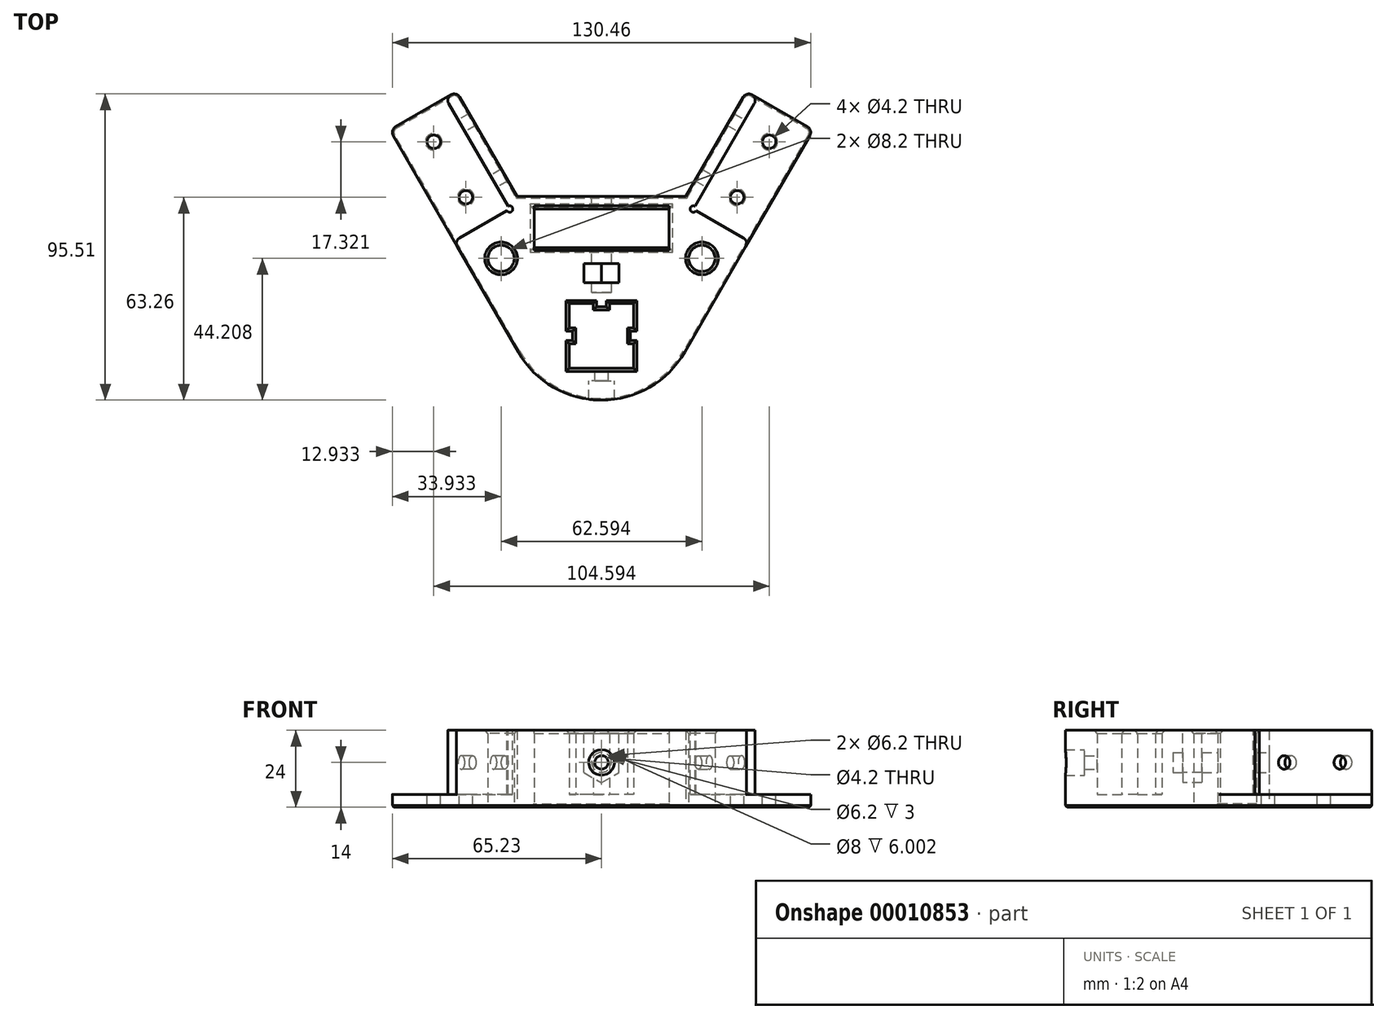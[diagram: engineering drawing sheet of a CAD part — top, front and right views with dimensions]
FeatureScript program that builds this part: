
annotation { "Feature Type Name" : "Feature", "Feature Type Description" : "" }
export const myFeature = defineFeature(function(context is Context, id is Id, definition is map)
    precondition{}
    {
        {
            var Q0;
            Q0=qCreatedBy(makeId("Top.planeOp"),FACE);
            var sketch = newSketch(context, id + "F0", { "sketchPlane" : qUnion([Q0])});
            skLineSegment(sketch, "E0.rect.bottom", {"start": v(10.05, -10.05) * mm, "end": v(-10.05, -10.05) * mm});
            skLineSegment(sketch, "E0.rect.top", {"start": v(10.05, 10.05) * mm, "end": v(-10.05, 10.05) * mm});
            skLineSegment(sketch, "E0.rect.left", {"start": v(10.05, -10.05) * mm, "end": v(10.05, 10.05) * mm});
            skLineSegment(sketch, "E0.rect.right", {"start": v(-10.05, -10.05) * mm, "end": v(-10.05, 10.05) * mm});
            skPoint(sketch, "E0.rect.middle", {"position": v(0, 0) * mm});
            skLineSegment(sketch, "E1", {"start": v(-10.05, -2.5) * mm, "end": v(-8.05, -2.5) * mm});
            skLineSegment(sketch, "E2", {"start": v(-8.05, -2.5) * mm, "end": v(-8.05, 2.5) * mm});
            skLineSegment(sketch, "E3", {"start": v(-8.05, 2.5) * mm, "end": v(-10.05, 2.5) * mm});
            skLineSegment(sketch, "E4", {"start": v(-2.5, 10.05) * mm, "end": v(-2.5, 8.05) * mm});
            skLineSegment(sketch, "E5", {"start": v(-2.5, 8.05) * mm, "end": v(2.5, 8.05) * mm});
            skLineSegment(sketch, "E6", {"start": v(2.5, 8.05) * mm, "end": v(2.5, 10.05) * mm});
            skLineSegment(sketch, "E7", {"start": v(10.05, 2.5) * mm, "end": v(8.05, 2.5) * mm});
            skLineSegment(sketch, "E8", {"start": v(8.05, 2.5) * mm, "end": v(8.05, -2.5) * mm});
            skLineSegment(sketch, "E9", {"start": v(8.05, -2.5) * mm, "end": v(10.05, -2.5) * mm});
            skLineSegment(sketch, "E10", {"start": v(-25.98, -5.05) * mm, "end": v(-65.96, 64.2) * mm});
            skLineSegment(sketch, "E11", {"start": v(-65.96, 64.2) * mm, "end": v(-45.17, 76.2) * mm});
            skLineSegment(sketch, "E12", {"start": v(-45.17, 76.2) * mm, "end": v(-25.17, 41.55) * mm});
            skLineSegment(sketch, "E13", {"start": v(-25.17, 41.55) * mm, "end": v(25.17, 41.55) * mm});
            skLineSegment(sketch, "E14", {"start": v(25.17, 41.55) * mm, "end": v(45.17, 76.2) * mm});
            skLineSegment(sketch, "E15", {"start": v(45.17, 76.2) * mm, "end": v(65.96, 64.2) * mm});
            skLineSegment(sketch, "E16", {"start": v(65.96, 64.2) * mm, "end": v(25.98, -5.05) * mm});
            skPoint(sketch, "E17.visualSharp", {"position": v(0, -50.05) * mm});
            skArc(sketch, "E17.filletArc", {"start": v(-25.98, -5.05) * mm, "mid": v(0, -20.05) * mm, "end": v(25.98, -5.05) * mm});
            skLineSegment(sketch, "E18", {"start": v(-48.64, 74.2) * mm, "end": v(-28.64, 39.55) * mm});
            skLineSegment(sketch, "E19", {"start": v(-28.64, 39.55) * mm, "end": v(-45.96, 29.55) * mm});
            skLineSegment(sketch, "E20", {"start": v(48.64, 74.2) * mm, "end": v(28.64, 39.55) * mm});
            skLineSegment(sketch, "E21", {"start": v(28.64, 39.55) * mm, "end": v(45.96, 29.55) * mm});
            skLineSegment(sketch, "E22", {"start": v(-28.64, 39.55) * mm, "end": v(-25.17, 41.55) * mm, "construction": true});
            skLineSegment(sketch, "E23", {"start": v(-57.3, 69.2) * mm, "end": v(-37.3, 34.55) * mm, "construction": true});
            skCircle(sketch, "E24", {"center": v(-52.3, 60.53) * mm, "radius": 2.1 * mm});
            skCircle(sketch, "E25", {"center": v(-42.3, 43.21) * mm, "radius": 2.1 * mm});
            skCircle(sketch, "E26", {"center": v(52.3, 60.53) * mm, "radius": 2.1 * mm});
            skCircle(sketch, "E27", {"center": v(42.3, 43.21) * mm, "radius": 2.1 * mm});
            skLineSegment(sketch, "E28", {"start": v(-21, 39.55) * mm, "end": v(21, 39.55) * mm});
            skLineSegment(sketch, "E29", {"start": v(21, 39.55) * mm, "end": v(21, 27.55) * mm});
            skLineSegment(sketch, "E30", {"start": v(10.05, 15.05) * mm, "end": v(-10.05, 15.05) * mm});
            skLineSegment(sketch, "E31", {"start": v(-21, 27.55) * mm, "end": v(-21, 39.55) * mm});
            skLineSegment(sketch, "E32", {"start": v(-21, 27.55) * mm, "end": v(-18.6, 17.84) * mm});
            skLineSegment(sketch, "E33", {"start": v(-18.6, 17.84) * mm, "end": v(-10.05, 15.05) * mm});
            skLineSegment(sketch, "E34", {"start": v(21, 27.55) * mm, "end": v(18.6, 17.84) * mm});
            skLineSegment(sketch, "E35", {"start": v(18.6, 17.84) * mm, "end": v(10.05, 15.05) * mm});
            skLineSegment(sketch, "E36", {"start": v(-37.3, 34.55) * mm, "end": v(-20.27, 5.06) * mm, "construction": true});
            skCircle(sketch, "E37", {"center": v(-31.3, 24.16) * mm, "radius": 4.1 * mm});
            skLineSegment(sketch, "E38", {"start": v(0, -71.13) * mm, "end": v(0, 233.1) * mm, "construction": true});
            skCircle(sketch, "E39", {"center": v(31.3, 24.16) * mm, "radius": 4.1 * mm});
            skLineSegment(sketch, "E40", {"start": v(-26.33, 43.55) * mm, "end": v(26.33, 43.55) * mm});
            skLineSegment(sketch, "E41", {"start": v(-21, 27.55) * mm, "end": v(21, 27.55) * mm});
            skLineSegment(sketch, "E42", {"start": v(-19.77, 22.55) * mm, "end": v(19.77, 22.55) * mm});
            skSolve(sketch);
        }
        {
            var Q0;
            {var subQ2=sQuery(id+"F0.wireOp",EDGE,"E13");Q0=makeQuery(id+"F0.imprint","IMPRINT",FACE,{"disambiguationData":[TD([[makeQuery(id+"F0.imprint","IMPRINT",EDGE,{"derivedFrom":subQ2}),1.0]])]});}
            var Q1;
            {var subQ16=sQuery(id+"F0.wireOp",EDGE,"E0.rect.bottom");Q1=makeQuery(id+"F0.imprint","IMPRINT",FACE,{"disambiguationData":[TD([[makeQuery(id+"F0.imprint","IMPRINT",EDGE,{"derivedFrom":subQ16}),1.0]])]});}
            var Q2;
            {var subQ1=sQuery(id+"F0.wireOp",EDGE,"E1");Q2=makeQuery(id+"F0.imprint","IMPRINT",FACE,{"disambiguationData":[TD([[makeQuery(id+"F0.imprint","IMPRINT",EDGE,{"derivedFrom":subQ1}),1.0]])]});}
            var Q3;
            {var subQ1=sQuery(id+"F0.wireOp",EDGE,"E4");Q3=makeQuery(id+"F0.imprint","IMPRINT",FACE,{"disambiguationData":[TD([[makeQuery(id+"F0.imprint","IMPRINT",EDGE,{"derivedFrom":subQ1}),1.0]])]});}
            var Q4;
            {var subQ1=sQuery(id+"F0.wireOp",EDGE,"E7");Q4=makeQuery(id+"F0.imprint","IMPRINT",FACE,{"disambiguationData":[TD([[makeQuery(id+"F0.imprint","IMPRINT",EDGE,{"derivedFrom":subQ1}),1.0]])]});}
            var Q5;
            {var subQ1=sQuery(id+"F0.wireOp",EDGE,"E41");Q5=makeQuery(id+"F0.imprint","IMPRINT",FACE,{"disambiguationData":[TD([[makeQuery(id+"F0.imprint","IMPRINT",EDGE,{"derivedFrom":subQ1}),-1.0]])]});}
            var Q6;
            Q6=makeQuery(id+"F0.imprint","IMPRINT",FACE,{"disambiguationData":[TD([[makeQuery(id+"F0.imprint","IMPRINT",EDGE,{"derivedFrom":sQuery(id+"F0.wireOp",EDGE,"E30")}),-1.0]])]});
            extrude(context, id + "F1", {"entities" : qUnion([Q0, Q1, Q2, Q3, Q4, Q5, Q6]), "depth" : 20 * mm});
        }
        {
            var Q0;
            {var subQ0=sQuery(id+"F0.wireOp",EDGE,"E20");Q0=makeQuery(id+"F0.imprint","IMPRINT",FACE,{"disambiguationData":[TD([[makeQuery(id+"F0.imprint","IMPRINT",EDGE,{"derivedFrom":subQ0}),1.0]])]});}
            var Q1;
            {var subQ16=sQuery(id+"F0.wireOp",EDGE,"E0.rect.bottom");Q1=makeQuery(id+"F0.imprint","IMPRINT",FACE,{"disambiguationData":[TD([[makeQuery(id+"F0.imprint","IMPRINT",EDGE,{"derivedFrom":subQ16}),1.0]])]});}
            var Q2;
            {var subQ11=sQuery(id+"F0.wireOp",EDGE,"E0.rect.bottom");Q2=makeQuery(id+"F0.imprint","IMPRINT",FACE,{"disambiguationData":[TD([[makeQuery(id+"F0.imprint","IMPRINT",EDGE,{"derivedFrom":subQ11}),-1.0]])]});}
            var Q3;
            {var subQ1=sQuery(id+"F0.wireOp",EDGE,"E18");Q3=makeQuery(id+"F0.imprint","IMPRINT",FACE,{"disambiguationData":[TD([[makeQuery(id+"F0.imprint","IMPRINT",EDGE,{"derivedFrom":subQ1}),-1.0]])]});}
            var Q4;
            {var subQ1=sQuery(id+"F0.wireOp",EDGE,"E4");Q4=makeQuery(id+"F0.imprint","IMPRINT",FACE,{"disambiguationData":[TD([[makeQuery(id+"F0.imprint","IMPRINT",EDGE,{"derivedFrom":subQ1}),1.0]])]});}
            var Q5;
            {var subQ1=sQuery(id+"F0.wireOp",EDGE,"E7");Q5=makeQuery(id+"F0.imprint","IMPRINT",FACE,{"disambiguationData":[TD([[makeQuery(id+"F0.imprint","IMPRINT",EDGE,{"derivedFrom":subQ1}),1.0]])]});}
            var Q6;
            {var subQ1=sQuery(id+"F0.wireOp",EDGE,"E1");Q6=makeQuery(id+"F0.imprint","IMPRINT",FACE,{"disambiguationData":[TD([[makeQuery(id+"F0.imprint","IMPRINT",EDGE,{"derivedFrom":subQ1}),1.0]])]});}
            var Q7;
            {var subQ2=sQuery(id+"F0.wireOp",EDGE,"E13");Q7=makeQuery(id+"F0.imprint","IMPRINT",FACE,{"disambiguationData":[TD([[makeQuery(id+"F0.imprint","IMPRINT",EDGE,{"derivedFrom":subQ2}),1.0]])]});}
            var Q8;
            {var subQ1=sQuery(id+"F0.wireOp",EDGE,"E41");Q8=makeQuery(id+"F0.imprint","IMPRINT",FACE,{"disambiguationData":[TD([[makeQuery(id+"F0.imprint","IMPRINT",EDGE,{"derivedFrom":subQ1}),-1.0]])]});}
            var Q9;
            Q9=makeQuery(id+"F0.imprint","IMPRINT",FACE,{"disambiguationData":[TD([[makeQuery(id+"F0.imprint","IMPRINT",EDGE,{"derivedFrom":sQuery(id+"F0.wireOp",EDGE,"E30")}),-1.0]])]});
            extrude(context, id + "F2", {"entities" : qUnion([Q0, Q1, Q2, Q3, Q4, Q5, Q6, Q7, Q8, Q9]), "operationType" : NewBodyOperationType.ADD, "oppositeDirection" : true, "depth" : 4 * mm});
        }
        {
            var Q0;
            {var subQ0=sQuery(id+"F0.wireOp",EDGE,"E40");Q0=makeQuery(id+"F2.boolean.opBoolean","MERGE",FACE,{"derivedFrom":[makeQuery(id+"F1.opExtrude","SWEPT_FACE",FACE,{"disambiguationData":[OSD([subQ0])]}),makeQuery(id+"F2.opExtrude","SWEPT_FACE",FACE,{"disambiguationData":[OSD([subQ0])]})]});}
            var sketch = newSketch(context, id + "F3", { "sketchPlane" : qUnion([Q0])});
            skCircle(sketch, "E43", {"center": v(0, 10) * mm, "radius": 3.1 * mm});
            skSolve(sketch);
        }
        {
            var Q0;
            Q0=makeQuery(id+"F3.imprint","IMPRINT",FACE,{"disambiguationData":[TD([[makeQuery(id+"F3.imprint","IMPRINT",EDGE,{"derivedFrom":sQuery(id+"F3.wireOp",EDGE,"E43")}),1.0]])]});
            extrude(context, id + "F4", {"entities" : qUnion([Q0]), "operationType" : NewBodyOperationType.REMOVE, "oppositeDirection" : true, "depth" : 30 * mm});
        }
        {
            var Q0;
            Q0=makeQuery(id+"F1.opExtrude","SWEPT_FACE",FACE,{"disambiguationData":[OSD([sQuery(id+"F0.wireOp",EDGE,"E20")])]});
            var sketch = newSketch(context, id + "F5", { "sketchPlane" : qUnion([Q0])});
            skCircle(sketch, "E44", {"center": v(58.57, 10) * mm, "radius": 2.1 * mm});
            skCircle(sketch, "E45", {"center": v(78.57, 10) * mm, "radius": 2.1 * mm});
            skSolve(sketch);
        }
        {
            var Q0;
            Q0=qSketchRegion(id+"F5",true);
            extrude(context, id + "F6", {"entities" : qUnion([Q0]), "operationType" : NewBodyOperationType.REMOVE, "oppositeDirection" : true, "depth" : 25 * mm});
        }
        {
            var Q0;
            Q0=makeQuery(id+"F1.opExtrude","SWEPT_FACE",FACE,{"disambiguationData":[OSD([sQuery(id+"F0.wireOp",EDGE,"E18")])]});
            var sketch = newSketch(context, id + "F7", { "sketchPlane" : qUnion([Q0])});
            skCircle(sketch, "E46", {"center": v(-78.57, 10) * mm, "radius": 2.1 * mm});
            skCircle(sketch, "E47", {"center": v(-58.57, 10) * mm, "radius": 2.1 * mm});
            skSolve(sketch);
        }
        {
            var Q0;
            Q0=qSketchRegion(id+"F7",true);
            extrude(context, id + "F8", {"entities" : qUnion([Q0]), "operationType" : NewBodyOperationType.REMOVE, "oppositeDirection" : true, "depth" : 25 * mm});
        }
        {
            var Q0;
            Q0=makeQuery(id+"F1.opExtrude","CAP_FACE",FACE,{"disambiguationData":[OSD([sQuery(id+"F0.wireOp",EDGE,"E0.rect.bottom"),sQuery(id+"F0.wireOp",EDGE,"E0.rect.top"),sQuery(id+"F0.wireOp",EDGE,"E0.rect.left"),sQuery(id+"F0.wireOp",EDGE,"E0.rect.right"),sQuery(id+"F0.wireOp",EDGE,"E1"),sQuery(id+"F0.wireOp",EDGE,"E2"),sQuery(id+"F0.wireOp",EDGE,"E3"),sQuery(id+"F0.wireOp",EDGE,"E4"),sQuery(id+"F0.wireOp",EDGE,"E5"),sQuery(id+"F0.wireOp",EDGE,"E6"),sQuery(id+"F0.wireOp",EDGE,"E7"),sQuery(id+"F0.wireOp",EDGE,"E8"),sQuery(id+"F0.wireOp",EDGE,"E9"),sQuery(id+"F0.wireOp",EDGE,"E10"),sQuery(id+"F0.wireOp",EDGE,"E11"),sQuery(id+"F0.wireOp",EDGE,"E12"),sQuery(id+"F0.wireOp",EDGE,"E14"),sQuery(id+"F0.wireOp",EDGE,"E15"),sQuery(id+"F0.wireOp",EDGE,"E16"),sQuery(id+"F0.wireOp",EDGE,"E17.filletArc"),sQuery(id+"F0.wireOp",EDGE,"E18"),sQuery(id+"F0.wireOp",EDGE,"E19"),sQuery(id+"F0.wireOp",EDGE,"E20"),sQuery(id+"F0.wireOp",EDGE,"E21"),sQuery(id+"F0.wireOp",EDGE,"E28"),sQuery(id+"F0.wireOp",EDGE,"E29"),sQuery(id+"F0.wireOp",EDGE,"E31"),sQuery(id+"F0.wireOp",EDGE,"E37"),sQuery(id+"F0.wireOp",EDGE,"E39"),sQuery(id+"F0.wireOp",EDGE,"E40"),sQuery(id+"F0.wireOp",EDGE,"E41")])],"isStart":false});
            var sketch = newSketch(context, id + "F9", { "sketchPlane" : qUnion([Q0])});
            skLineSegment(sketch, "E48.rect.bottom", {"start": v(5.5, 16.55) * mm, "end": v(-5.5, 16.55) * mm});
            skLineSegment(sketch, "E48.rect.top", {"start": v(5.5, 22.55) * mm, "end": v(-5.5, 22.55) * mm});
            skLineSegment(sketch, "E48.rect.left", {"start": v(5.5, 16.55) * mm, "end": v(5.5, 22.55) * mm});
            skLineSegment(sketch, "E48.rect.right", {"start": v(-5.5, 16.55) * mm, "end": v(-5.5, 22.55) * mm});
            skPoint(sketch, "E48.rect.middle", {"position": v(0, 19.55) * mm});
            skSolve(sketch);
        }
        {
            var Q0;
            Q0=makeQuery(id+"F9.imprint","IMPRINT",FACE,{"disambiguationData":[TD([[makeQuery(id+"F9.imprint","IMPRINT",EDGE,{"derivedFrom":sQuery(id+"F9.wireOp",EDGE,"E48.rect.bottom")}),-1.0]])]});
            extrude(context, id + "F10", {"entities" : qUnion([Q0]), "operationType" : NewBodyOperationType.REMOVE, "oppositeDirection" : true, "depth" : 10.5 * mm});
        }
        {
            var Q0;
            Q0=makeQuery(id+"F10.boolean.opBoolean","COPY",FACE,{"derivedFrom":makeQuery(id+"F10.opExtrude","SWEPT_FACE",FACE,{"disambiguationData":[OSD([sQuery(id+"F9.wireOp",EDGE,"E48.rect.bottom")])]})});
            var sketch = newSketch(context, id + "F11", { "sketchPlane" : qUnion([Q0])});
            skCircle(sketch, "E49.cCircle", {"center": v(0, 10) * mm, "radius": 5.5 * mm, "construction": true});
            skLineSegment(sketch, "E49.0", {"start": v(5.5, 6.82) * mm, "end": v(0, 3.65) * mm});
            skLineSegment(sketch, "E49.1", {"start": v(0, 3.65) * mm, "end": v(-5.5, 6.82) * mm});
            skLineSegment(sketch, "E49.2", {"start": v(-5.5, 6.82) * mm, "end": v(-5.5, 13.18) * mm});
            skLineSegment(sketch, "E49.3", {"start": v(-5.5, 13.18) * mm, "end": v(0, 16.35) * mm});
            skLineSegment(sketch, "E49.4", {"start": v(0, 16.35) * mm, "end": v(5.5, 13.18) * mm});
            skLineSegment(sketch, "E49.5", {"start": v(5.5, 13.18) * mm, "end": v(5.5, 6.82) * mm});
            skPoint(sketch, "E49.0.midPoint", {"position": v(2.75, 5.24) * mm});
            skSolve(sketch);
        }
        {
            var Q0;
            Q0=qSketchRegion(id+"F11",true);
            var Q1;
            Q1=makeQuery(id+"F10.boolean.opBoolean","COPY",FACE,{"derivedFrom":makeQuery(id+"F10.opExtrude","SWEPT_FACE",FACE,{"disambiguationData":[OSD([sQuery(id+"F9.wireOp",EDGE,"E48.rect.top")])]})});
            extrude(context, id + "F12", {"entities" : qUnion([Q0]), "operationType" : NewBodyOperationType.REMOVE, "endBound" : BoundingType.UP_TO_SURFACE, "endBoundEntityFace" : qUnion([Q1]), "depth" : 25 * mm});
        }
        {
            var Q0;
            Q0=makeQuery(id+"F1.opExtrude","CAP_FACE",FACE,{"disambiguationData":[OSD([sQuery(id+"F0.wireOp",EDGE,"E0.rect.bottom"),sQuery(id+"F0.wireOp",EDGE,"E0.rect.top"),sQuery(id+"F0.wireOp",EDGE,"E0.rect.left"),sQuery(id+"F0.wireOp",EDGE,"E0.rect.right"),sQuery(id+"F0.wireOp",EDGE,"E1"),sQuery(id+"F0.wireOp",EDGE,"E2"),sQuery(id+"F0.wireOp",EDGE,"E3"),sQuery(id+"F0.wireOp",EDGE,"E4"),sQuery(id+"F0.wireOp",EDGE,"E5"),sQuery(id+"F0.wireOp",EDGE,"E6"),sQuery(id+"F0.wireOp",EDGE,"E7"),sQuery(id+"F0.wireOp",EDGE,"E8"),sQuery(id+"F0.wireOp",EDGE,"E9"),sQuery(id+"F0.wireOp",EDGE,"E10"),sQuery(id+"F0.wireOp",EDGE,"E11"),sQuery(id+"F0.wireOp",EDGE,"E12"),sQuery(id+"F0.wireOp",EDGE,"E14"),sQuery(id+"F0.wireOp",EDGE,"E15"),sQuery(id+"F0.wireOp",EDGE,"E16"),sQuery(id+"F0.wireOp",EDGE,"E17.filletArc"),sQuery(id+"F0.wireOp",EDGE,"E18"),sQuery(id+"F0.wireOp",EDGE,"E19"),sQuery(id+"F0.wireOp",EDGE,"E20"),sQuery(id+"F0.wireOp",EDGE,"E21"),sQuery(id+"F0.wireOp",EDGE,"E28"),sQuery(id+"F0.wireOp",EDGE,"E29"),sQuery(id+"F0.wireOp",EDGE,"E31"),sQuery(id+"F0.wireOp",EDGE,"E37"),sQuery(id+"F0.wireOp",EDGE,"E39"),sQuery(id+"F0.wireOp",EDGE,"E40"),sQuery(id+"F0.wireOp",EDGE,"E41")])],"isStart":false});
            var sketch = newSketch(context, id + "F13", { "sketchPlane" : qUnion([Q0])});
            skCircle(sketch, "E50", {"center": v(28.64, 39.55) * mm, "radius": 1 * mm});
            skCircle(sketch, "E51", {"center": v(-28.64, 39.55) * mm, "radius": 1 * mm});
            skSolve(sketch);
        }
        {
            var Q0;
            {var subQ1=sQuery(id+"F13.wireOp",EDGE,"E50");var subQ3=makeQuery(id+"F1.opExtrude","CAP_EDGE",EDGE,{"disambiguationData":[OSD([sQuery(id+"F0.wireOp",EDGE,"E20")])],"isStart":false});var subQ5=makeQuery(id+"F13.imprint","INTERSECT",VERTEX,{"derivedFrom":[subQ3,subQ1]});Q0=makeQuery(id+"F13.imprint","IMPRINT",FACE,{"disambiguationData":[TD([[makeQuery(id+"F13.imprint","IMPRINT",EDGE,{"disambiguationData":[TD([[subQ5,-1.0]])],"derivedFrom":subQ1}),1.0]])]});}
            var Q1;
            {var subQ1=sQuery(id+"F13.wireOp",EDGE,"E51");var subQ3=makeQuery(id+"F1.opExtrude","CAP_EDGE",EDGE,{"disambiguationData":[OSD([sQuery(id+"F0.wireOp",EDGE,"E18")])],"isStart":false});var subQ5=makeQuery(id+"F13.imprint","INTERSECT",VERTEX,{"derivedFrom":[subQ3,subQ1]});Q1=makeQuery(id+"F13.imprint","IMPRINT",FACE,{"disambiguationData":[TD([[makeQuery(id+"F13.imprint","IMPRINT",EDGE,{"disambiguationData":[TD([[subQ5,1.0]])],"derivedFrom":subQ1}),1.0]])]});}
            var Q2;
            {var subQ0=sQuery(id+"F0.wireOp",EDGE,"E15");var subQ1=sQuery(id+"F0.wireOp",EDGE,"E16");var subQ2=sQuery(id+"F0.wireOp",EDGE,"E26");var subQ3=sQuery(id+"F0.wireOp",EDGE,"E27");Q2=makeQuery(id+"F2.boolean.opBoolean","SPLIT",FACE,{"disambiguationData":[TD([makeQuery(id+"F1.opExtrude","SWEPT_FACE",FACE,{"disambiguationData":[OSD([subQ0])]})])],"derivedFrom":makeQuery(id+"F2.opExtrude","CAP_FACE",FACE,{"disambiguationData":[OSD([sQuery(id+"F0.wireOp",EDGE,"E10"),sQuery(id+"F0.wireOp",EDGE,"E11"),sQuery(id+"F0.wireOp",EDGE,"E12"),sQuery(id+"F0.wireOp",EDGE,"E14"),subQ0,subQ1,sQuery(id+"F0.wireOp",EDGE,"E17.filletArc"),sQuery(id+"F0.wireOp",EDGE,"E24"),sQuery(id+"F0.wireOp",EDGE,"E25"),subQ2,subQ3,sQuery(id+"F0.wireOp",EDGE,"E28"),sQuery(id+"F0.wireOp",EDGE,"E29"),sQuery(id+"F0.wireOp",EDGE,"E31"),sQuery(id+"F0.wireOp",EDGE,"E40"),sQuery(id+"F0.wireOp",EDGE,"E41")])],"isStart":true})});}
            extrude(context, id + "F14", {"entities" : qUnion([Q0, Q1]), "operationType" : NewBodyOperationType.REMOVE, "endBound" : BoundingType.UP_TO_SURFACE, "oppositeDirection" : true, "endBoundEntityFace" : qUnion([Q2]), "depth" : 25 * mm});
        }
        {
            var Q0;
            Q0=makeQuery(id+"F1.opExtrude","SWEPT_EDGE",EDGE,{"disambiguationData":[OSD([sQuery(id+"F0.wireOp",EDGE,"E11"),sQuery(id+"F0.wireOp",EDGE,"E18")])]});
            var Q1;
            {var subQ0=sQuery(id+"F0.wireOp",EDGE,"E11");var subQ1=sQuery(id+"F0.wireOp",EDGE,"E12");Q1=makeQuery(id+"F2.boolean.opBoolean","MERGE",EDGE,{"derivedFrom":[makeQuery(id+"F1.opExtrude","SWEPT_EDGE",EDGE,{"disambiguationData":[OSD([subQ0,subQ1])]}),makeQuery(id+"F2.opExtrude","SWEPT_EDGE",EDGE,{"disambiguationData":[OSD([subQ0,subQ1])]})]});}
            var Q2;
            Q2=makeQuery(id+"F1.opExtrude","SWEPT_EDGE",EDGE,{"disambiguationData":[OSD([sQuery(id+"F0.wireOp",EDGE,"E10"),sQuery(id+"F0.wireOp",EDGE,"E19")])]});
            var Q3;
            Q3=makeQuery(id+"F14.boolean.opBoolean","COPY",EDGE,{"derivedFrom":makeQuery(id+"F14.opExtrude","SWEPT_EDGE",EDGE,{"disambiguationData":[OSD([sQuery(id+"F0.wireOp",EDGE,"E19"),sQuery(id+"F13.wireOp",EDGE,"E51")])]})});
            var Q4;
            Q4=makeQuery(id+"F14.boolean.opBoolean","COPY",EDGE,{"derivedFrom":makeQuery(id+"F14.opExtrude","SWEPT_EDGE",EDGE,{"disambiguationData":[OSD([sQuery(id+"F0.wireOp",EDGE,"E18"),sQuery(id+"F13.wireOp",EDGE,"E51")])]})});
            var Q5;
            Q5=makeQuery(id+"F2.opExtrude","SWEPT_EDGE",EDGE,{"disambiguationData":[OSD([sQuery(id+"F0.wireOp",EDGE,"E10"),sQuery(id+"F0.wireOp",EDGE,"E11")])]});
            var Q6;
            {var subQ0=sQuery(id+"F0.wireOp",EDGE,"E14");var subQ1=sQuery(id+"F0.wireOp",EDGE,"E15");Q6=makeQuery(id+"F2.boolean.opBoolean","MERGE",EDGE,{"derivedFrom":[makeQuery(id+"F1.opExtrude","SWEPT_EDGE",EDGE,{"disambiguationData":[OSD([subQ0,subQ1])]}),makeQuery(id+"F2.opExtrude","SWEPT_EDGE",EDGE,{"disambiguationData":[OSD([subQ0,subQ1])]})]});}
            var Q7;
            Q7=makeQuery(id+"F1.opExtrude","SWEPT_EDGE",EDGE,{"disambiguationData":[OSD([sQuery(id+"F0.wireOp",EDGE,"E15"),sQuery(id+"F0.wireOp",EDGE,"E20")])]});
            var Q8;
            Q8=makeQuery(id+"F2.opExtrude","SWEPT_EDGE",EDGE,{"disambiguationData":[OSD([sQuery(id+"F0.wireOp",EDGE,"E15"),sQuery(id+"F0.wireOp",EDGE,"E16")])]});
            var Q9;
            Q9=makeQuery(id+"F1.opExtrude","SWEPT_EDGE",EDGE,{"disambiguationData":[OSD([sQuery(id+"F0.wireOp",EDGE,"E16"),sQuery(id+"F0.wireOp",EDGE,"E21")])]});
            var Q10;
            Q10=makeQuery(id+"F14.boolean.opBoolean","COPY",EDGE,{"derivedFrom":makeQuery(id+"F14.opExtrude","SWEPT_EDGE",EDGE,{"disambiguationData":[OSD([sQuery(id+"F0.wireOp",EDGE,"E21"),sQuery(id+"F13.wireOp",EDGE,"E50")])]})});
            var Q11;
            Q11=makeQuery(id+"F14.boolean.opBoolean","COPY",EDGE,{"derivedFrom":makeQuery(id+"F14.opExtrude","SWEPT_EDGE",EDGE,{"disambiguationData":[OSD([sQuery(id+"F0.wireOp",EDGE,"E20"),sQuery(id+"F13.wireOp",EDGE,"E50")])]})});
            fillet(context, id + "F15", {"entities" : qUnion([Q0, Q1, Q2, Q3, Q4, Q5, Q6, Q7, Q8, Q9, Q10, Q11]), "radius" : 2 * mm, "tangentPropagation" : true, "allowEdgeOverflow" : false});
        }
        {
            var Q0;
            Q0=makeQuery(id+"F10.boolean.opBoolean","COPY",EDGE,{"derivedFrom":makeQuery(id+"F10.opExtrude","CAP_EDGE",EDGE,{"disambiguationData":[OSD([sQuery(id+"F9.wireOp",EDGE,"E48.rect.top")])],"isStart":true})});
            var Q1;
            Q1=makeQuery(id+"F10.boolean.opBoolean","COPY",EDGE,{"derivedFrom":makeQuery(id+"F10.opExtrude","CAP_EDGE",EDGE,{"disambiguationData":[OSD([sQuery(id+"F9.wireOp",EDGE,"E48.rect.left")])],"isStart":true})});
            var Q2;
            Q2=makeQuery(id+"F10.boolean.opBoolean","COPY",EDGE,{"derivedFrom":makeQuery(id+"F10.opExtrude","CAP_EDGE",EDGE,{"disambiguationData":[OSD([sQuery(id+"F9.wireOp",EDGE,"E48.rect.bottom")])],"isStart":true})});
            var Q3;
            Q3=makeQuery(id+"F10.boolean.opBoolean","COPY",EDGE,{"derivedFrom":makeQuery(id+"F10.opExtrude","CAP_EDGE",EDGE,{"disambiguationData":[OSD([sQuery(id+"F9.wireOp",EDGE,"E48.rect.right")])],"isStart":true})});
            var Q4;
            {var subQ0=sQuery(id+"F0.wireOp",EDGE,"E0.rect.top");Q4=makeQuery(id+"F1.opExtrude","CAP_EDGE",EDGE,{"disambiguationData":[OSD([subQ0]),TDD([makeQuery(id+"F0.imprint","IMPRINT",EDGE,{"disambiguationData":[TD([[makeQuery(id+"F0.imprint","INTERSECT",VERTEX,{"derivedFrom":[subQ0,sQuery(id+"F0.wireOp",EDGE,"E0.rect.right")]}),1.0]])],"derivedFrom":subQ0})])],"isStart":false});}
            var Q5;
            Q5=makeQuery(id+"F1.opExtrude","CAP_EDGE",EDGE,{"disambiguationData":[OSD([sQuery(id+"F0.wireOp",EDGE,"E4")])],"isStart":false});
            var Q6;
            Q6=makeQuery(id+"F1.opExtrude","CAP_EDGE",EDGE,{"disambiguationData":[OSD([sQuery(id+"F0.wireOp",EDGE,"E5")])],"isStart":false});
            var Q7;
            Q7=makeQuery(id+"F1.opExtrude","CAP_EDGE",EDGE,{"disambiguationData":[OSD([sQuery(id+"F0.wireOp",EDGE,"E6")])],"isStart":false});
            var Q8;
            {var subQ0=sQuery(id+"F0.wireOp",EDGE,"E0.rect.top");Q8=makeQuery(id+"F1.opExtrude","CAP_EDGE",EDGE,{"disambiguationData":[OSD([subQ0]),TDD([makeQuery(id+"F0.imprint","IMPRINT",EDGE,{"disambiguationData":[TD([[makeQuery(id+"F0.imprint","INTERSECT",VERTEX,{"derivedFrom":[subQ0,sQuery(id+"F0.wireOp",EDGE,"E0.rect.left")]}),-1.0]])],"derivedFrom":subQ0})])],"isStart":false});}
            var Q9;
            {var subQ0=sQuery(id+"F0.wireOp",EDGE,"E0.rect.left");Q9=makeQuery(id+"F1.opExtrude","CAP_EDGE",EDGE,{"disambiguationData":[OSD([subQ0]),TDD([makeQuery(id+"F0.imprint","IMPRINT",EDGE,{"disambiguationData":[TD([[makeQuery(id+"F0.imprint","INTERSECT",VERTEX,{"derivedFrom":[sQuery(id+"F0.wireOp",EDGE,"E0.rect.top"),subQ0]}),1.0]])],"derivedFrom":subQ0})])],"isStart":false});}
            var Q10;
            Q10=makeQuery(id+"F1.opExtrude","CAP_EDGE",EDGE,{"disambiguationData":[OSD([sQuery(id+"F0.wireOp",EDGE,"E7")])],"isStart":false});
            var Q11;
            Q11=makeQuery(id+"F1.opExtrude","CAP_EDGE",EDGE,{"disambiguationData":[OSD([sQuery(id+"F0.wireOp",EDGE,"E8")])],"isStart":false});
            var Q12;
            Q12=makeQuery(id+"F1.opExtrude","CAP_EDGE",EDGE,{"disambiguationData":[OSD([sQuery(id+"F0.wireOp",EDGE,"E9")])],"isStart":false});
            var Q13;
            {var subQ0=sQuery(id+"F0.wireOp",EDGE,"E0.rect.left");Q13=makeQuery(id+"F1.opExtrude","CAP_EDGE",EDGE,{"disambiguationData":[OSD([subQ0]),TDD([makeQuery(id+"F0.imprint","IMPRINT",EDGE,{"disambiguationData":[TD([[makeQuery(id+"F0.imprint","INTERSECT",VERTEX,{"derivedFrom":[sQuery(id+"F0.wireOp",EDGE,"E0.rect.bottom"),subQ0]}),-1.0]])],"derivedFrom":subQ0})])],"isStart":false});}
            var Q14;
            Q14=makeQuery(id+"F1.opExtrude","CAP_EDGE",EDGE,{"disambiguationData":[OSD([sQuery(id+"F0.wireOp",EDGE,"E0.rect.bottom")])],"isStart":false});
            var Q15;
            {var subQ0=sQuery(id+"F0.wireOp",EDGE,"E0.rect.right");Q15=makeQuery(id+"F1.opExtrude","CAP_EDGE",EDGE,{"disambiguationData":[OSD([subQ0]),TDD([makeQuery(id+"F0.imprint","IMPRINT",EDGE,{"disambiguationData":[TD([[makeQuery(id+"F0.imprint","INTERSECT",VERTEX,{"derivedFrom":[sQuery(id+"F0.wireOp",EDGE,"E0.rect.bottom"),subQ0]}),-1.0]])],"derivedFrom":subQ0})])],"isStart":false});}
            var Q16;
            Q16=makeQuery(id+"F1.opExtrude","CAP_EDGE",EDGE,{"disambiguationData":[OSD([sQuery(id+"F0.wireOp",EDGE,"E1")])],"isStart":false});
            var Q17;
            {var subQ0=sQuery(id+"F0.wireOp",EDGE,"E0.rect.right");Q17=makeQuery(id+"F1.opExtrude","CAP_EDGE",EDGE,{"disambiguationData":[OSD([subQ0]),TDD([makeQuery(id+"F0.imprint","IMPRINT",EDGE,{"disambiguationData":[TD([[makeQuery(id+"F0.imprint","INTERSECT",VERTEX,{"derivedFrom":[sQuery(id+"F0.wireOp",EDGE,"E0.rect.top"),subQ0]}),1.0]])],"derivedFrom":subQ0})])],"isStart":false});}
            var Q18;
            Q18=makeQuery(id+"F1.opExtrude","CAP_EDGE",EDGE,{"disambiguationData":[OSD([sQuery(id+"F0.wireOp",EDGE,"E3")])],"isStart":false});
            var Q19;
            Q19=makeQuery(id+"F1.opExtrude","CAP_EDGE",EDGE,{"disambiguationData":[OSD([sQuery(id+"F0.wireOp",EDGE,"E2")])],"isStart":false});
            var Q20;
            Q20=makeQuery(id+"F1.opExtrude","CAP_EDGE",EDGE,{"disambiguationData":[OSD([sQuery(id+"F0.wireOp",EDGE,"E39")])],"isStart":false});
            var Q21;
            Q21=makeQuery(id+"F1.opExtrude","CAP_EDGE",EDGE,{"disambiguationData":[OSD([sQuery(id+"F0.wireOp",EDGE,"E37")])],"isStart":false});
            var Q22;
            Q22=makeQuery(id+"F1.opExtrude","CAP_EDGE",EDGE,{"disambiguationData":[OSD([sQuery(id+"F0.wireOp",EDGE,"E28")])],"isStart":false});
            var Q23;
            Q23=makeQuery(id+"F1.opExtrude","CAP_EDGE",EDGE,{"disambiguationData":[OSD([sQuery(id+"F0.wireOp",EDGE,"E41")])],"isStart":false});
            var Q24;
            Q24=makeQuery(id+"F2.opExtrude","CAP_EDGE",EDGE,{"disambiguationData":[OSD([sQuery(id+"F0.wireOp",EDGE,"E41")])],"isStart":false});
            var Q25;
            Q25=makeQuery(id+"F2.opExtrude","CAP_EDGE",EDGE,{"disambiguationData":[OSD([sQuery(id+"F0.wireOp",EDGE,"E28")])],"isStart":false});
            chamfer(context, id + "F16", {"entities" : qUnion([Q0, Q1, Q2, Q3, Q4, Q5, Q6, Q7, Q8, Q9, Q10, Q11, Q12, Q13, Q14, Q15, Q16, Q17, Q18, Q19, Q20, Q21, Q22, Q23, Q24, Q25]), "width" : 1 * mm, "tangentPropagation" : true});
        }
        {
            var Q0;
            Q0=qCreatedBy(makeId("Front.planeOp"),FACE);
            var sketch = newSketch(context, id + "F17", { "sketchPlane" : qUnion([Q0])});
            skCircle(sketch, "E52", {"center": v(0, 10) * mm, "radius": 2.1 * mm});
            skCircle(sketch, "E53", {"center": v(0, 10) * mm, "radius": 4 * mm});
            skSolve(sketch);
        }
        {
            var Q0;
            Q0=makeQuery(id+"F17.imprint","IMPRINT",FACE,{"disambiguationData":[TD([[makeQuery(id+"F17.imprint","IMPRINT",EDGE,{"derivedFrom":sQuery(id+"F17.wireOp",EDGE,"E52")}),1.0]])]});
            extrude(context, id + "F18", {"entities" : qUnion([Q0]), "operationType" : NewBodyOperationType.REMOVE, "endBound" : BoundingType.THROUGH_ALL, "depth" : 25 * mm});
        }
        {
            var Q0;
            Q0=makeQuery(id+"F17.imprint","IMPRINT",FACE,{"disambiguationData":[TD([[makeQuery(id+"F17.imprint","IMPRINT",EDGE,{"derivedFrom":sQuery(id+"F17.wireOp",EDGE,"E52")}),-1.0]])]});
            extrude(context, id + "F19", {"entities" : qUnion([Q0]), "operationType" : NewBodyOperationType.REMOVE, "depth" : 25 * mm, "hasSecondDirection" : true, "secondDirectionOppositeDirection" : false, "secondDirectionDepth" : 14.05 * mm});
        }
        {
            var Q0;
            Q0=makeQuery(id+"F2.opExtrude","CAP_FACE",FACE,{"disambiguationData":[OSD([sQuery(id+"F0.wireOp",EDGE,"E10"),sQuery(id+"F0.wireOp",EDGE,"E11"),sQuery(id+"F0.wireOp",EDGE,"E12"),sQuery(id+"F0.wireOp",EDGE,"E14"),sQuery(id+"F0.wireOp",EDGE,"E15"),sQuery(id+"F0.wireOp",EDGE,"E16"),sQuery(id+"F0.wireOp",EDGE,"E17.filletArc"),sQuery(id+"F0.wireOp",EDGE,"E24"),sQuery(id+"F0.wireOp",EDGE,"E25"),sQuery(id+"F0.wireOp",EDGE,"E26"),sQuery(id+"F0.wireOp",EDGE,"E27"),sQuery(id+"F0.wireOp",EDGE,"E28"),sQuery(id+"F0.wireOp",EDGE,"E29"),sQuery(id+"F0.wireOp",EDGE,"E31"),sQuery(id+"F0.wireOp",EDGE,"E37"),sQuery(id+"F0.wireOp",EDGE,"E39"),sQuery(id+"F0.wireOp",EDGE,"E40"),sQuery(id+"F0.wireOp",EDGE,"E41")])],"isStart":false});
            chamfer(context, id + "F20", {"entities" : qUnion([Q0]), "width" : 0.5 * mm, "tangentPropagation" : true});
        }
    });
